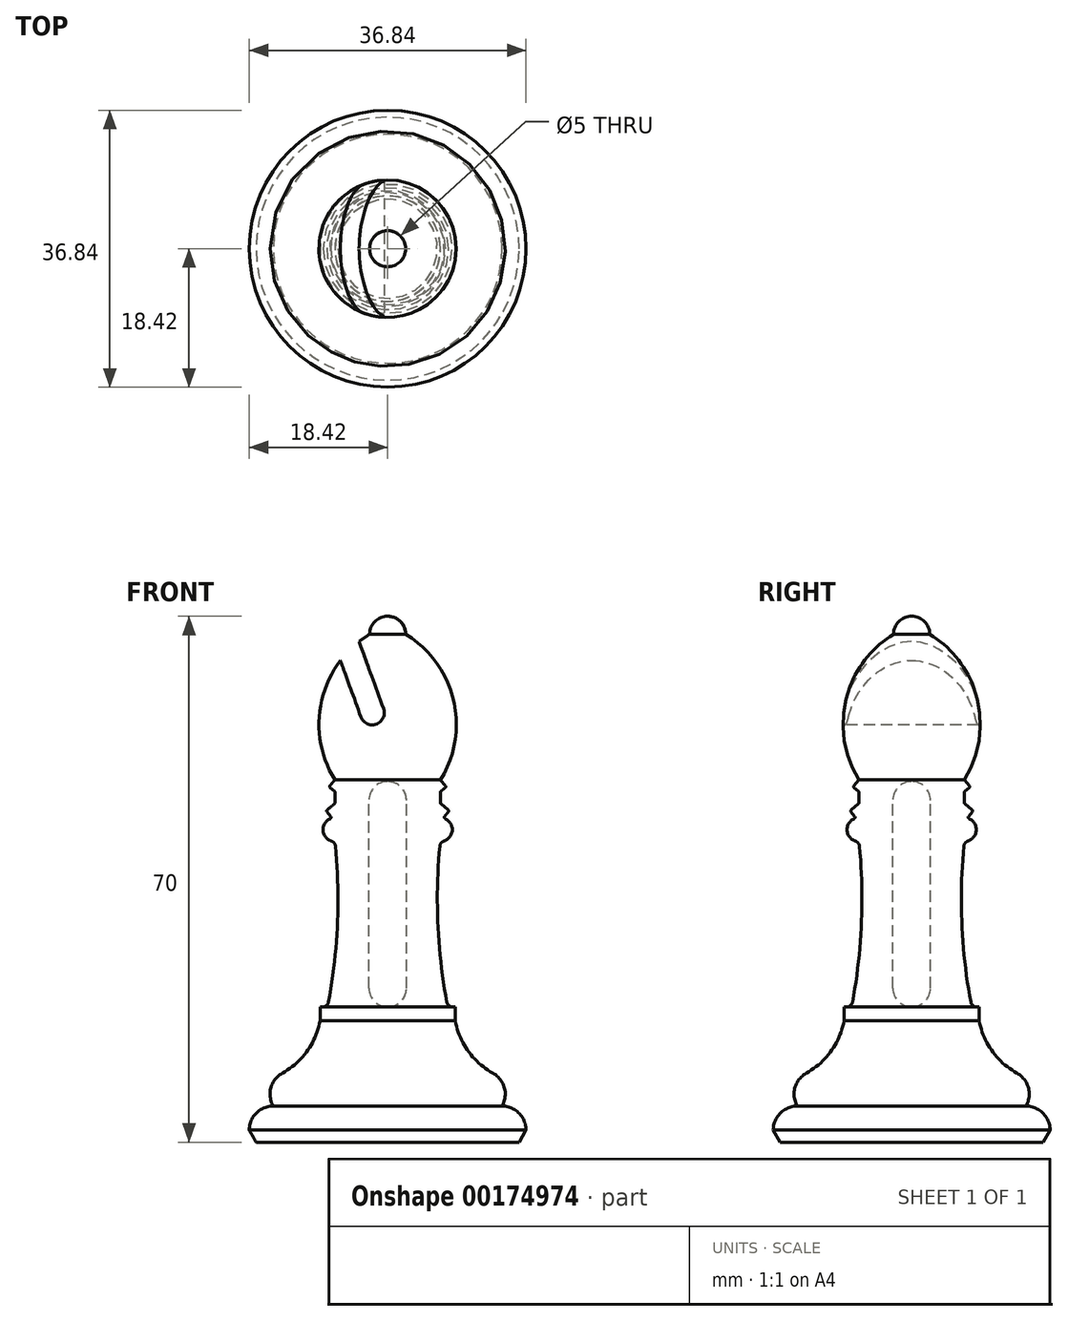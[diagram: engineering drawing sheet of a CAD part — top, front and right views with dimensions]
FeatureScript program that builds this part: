
annotation { "Feature Type Name" : "Feature", "Feature Type Description" : "" }
export const myFeature = defineFeature(function(context is Context, id is Id, definition is map)
    precondition{}
    {
        {
            var Q0;
            Q0=qCreatedBy(makeId("Front.planeOp"),FACE);
            var sketch = newSketch(context, id + "F0", { "sketchPlane" : qUnion([Q0])});
            skLineSegment(sketch, "E0", {"start": v(0, 0) * mm, "end": v(17.5, 0) * mm});
            skLineSegment(sketch, "E1", {"start": v(0, 0) * mm, "end": v(0, 95) * mm, "construction": true});
            skLineSegment(sketch, "E2", {"start": v(0, 18) * mm, "end": v(9, 18) * mm, "construction": true});
            skLineSegment(sketch, "E3", {"start": v(14.4, 40) * mm, "end": v(0, 40) * mm, "construction": true});
            skLineSegment(sketch, "E4", {"start": v(0, 60) * mm, "end": v(12.7, 60) * mm, "construction": true});
            skLineSegment(sketch, "E5", {"start": v(0, 64.34) * mm, "end": v(14.8, 64.34) * mm, "construction": true});
            skLineSegment(sketch, "E6", {"start": v(17.5, 0) * mm, "end": v(18.42, 1.6) * mm});
            skArc(sketch, "E7", {"start": v(18.42, 1.6) * mm, "mid": v(17.49, 3.86) * mm, "end": v(15.22, 4.8) * mm});
            skLineSegment(sketch, "E8", {"start": v(9, 18) * mm, "end": v(9, 16.15) * mm});
            skArc(sketch, "E9", {"start": v(9, 16.15) * mm, "mid": v(10.72, 12.11) * mm, "end": v(14, 9.2) * mm});
            skArc(sketch, "E10", {"start": v(15.22, 4.8) * mm, "mid": v(15.54, 7.26) * mm, "end": v(14, 9.2) * mm});
            skLineSegment(sketch, "E11", {"start": v(9, 18) * mm, "end": v(8, 18) * mm});
            skArc(sketch, "E12", {"start": v(7, 40) * mm, "mid": v(6.69, 28.96) * mm, "end": v(8, 18) * mm});
            skArc(sketch, "E13", {"start": v(7, 40) * mm, "mid": v(8.59, 41.4) * mm, "end": v(7.4, 43.15) * mm});
            skLineSegment(sketch, "E14", {"start": v(7.4, 43.15) * mm, "end": v(8.2, 44.1) * mm});
            skLineSegment(sketch, "E15", {"start": v(8.2, 44.1) * mm, "end": v(7, 45.1) * mm});
            skLineSegment(sketch, "E16", {"start": v(7, 45.1) * mm, "end": v(7, 46.63) * mm});
            skLineSegment(sketch, "E17", {"start": v(7, 46.63) * mm, "end": v(7.8, 47.3) * mm});
            skLineSegment(sketch, "E18", {"start": v(7.8, 47.3) * mm, "end": v(7, 48.26) * mm});
            skLineSegment(sketch, "E19", {"start": v(3.2, 63.2) * mm, "end": v(0, 63.2) * mm});
            skLineSegment(sketch, "E20", {"start": v(0, 63.2) * mm, "end": v(0, 0) * mm});
            skArc(sketch, "E21", {"start": v(7, 48.26) * mm, "mid": v(6.78, 56.16) * mm, "end": v(3.2, 63.2) * mm});
            skSolve(sketch);
        }
        {
            var Q0;
            Q0=qSketchRegion(id+"F0",true);
            var Q1;
            Q1=sQuery(id+"F0.wireOp",EDGE,"E1");
            revolve(context, id + "F1", {"entities" : qUnion([Q0]), "axis" : qUnion([Q1]), "revolveType" : RevolveType.FULL});
        }
        {
            var Q0;
            Q0=makeQuery(id+"F1.opRevolve","SWEPT_EDGE",EDGE,{"disambiguationData":[OSD([sQuery(id+"F0.wireOp",EDGE,"E12"),sQuery(id+"F0.wireOp",EDGE,"E13")])]});
            var Q1;
            Q1=makeQuery(id+"F1.opRevolve","SWEPT_EDGE",EDGE,{"disambiguationData":[OSD([sQuery(id+"F0.wireOp",EDGE,"E11"),sQuery(id+"F0.wireOp",EDGE,"E12")])]});
            fillet(context, id + "F2", {"entities" : qUnion([Q0, Q1]), "radius" : .8 * mm, "tangentPropagation" : true, "allowEdgeOverflow" : false});
        }
        {
            var Q0;
            Q0=makeQuery(id+"F1.opRevolve","SWEPT_EDGE",EDGE,{"disambiguationData":[OSD([sQuery(id+"F0.wireOp",EDGE,"E17"),sQuery(id+"F0.wireOp",EDGE,"E18")])]});
            var Q1;
            Q1=makeQuery(id+"F1.opRevolve","SWEPT_EDGE",EDGE,{"disambiguationData":[OSD([sQuery(id+"F0.wireOp",EDGE,"E14"),sQuery(id+"F0.wireOp",EDGE,"E15")])]});
            var Q2;
            Q2=makeQuery(id+"F1.opRevolve","SWEPT_EDGE",EDGE,{"disambiguationData":[OSD([sQuery(id+"F0.wireOp",EDGE,"OAx1KunF-KjKq-zgV9-Glhn-Sdbq04AqaJ7j"),sQuery(id+"F0.wireOp",EDGE,"E18")])]});
            var Q3;
            Q3=makeQuery(id+"F1.opRevolve","SWEPT_EDGE",EDGE,{"disambiguationData":[OSD([sQuery(id+"F0.wireOp",EDGE,"E16"),sQuery(id+"F0.wireOp",EDGE,"E17")])]});
            var Q4;
            Q4=makeQuery(id+"F1.opRevolve","SWEPT_EDGE",EDGE,{"disambiguationData":[OSD([sQuery(id+"F0.wireOp",EDGE,"E15"),sQuery(id+"F0.wireOp",EDGE,"E16")])]});
            var Q5;
            Q5=makeQuery(id+"F1.opRevolve","SWEPT_EDGE",EDGE,{"disambiguationData":[OSD([sQuery(id+"F0.wireOp",EDGE,"E13"),sQuery(id+"F0.wireOp",EDGE,"E14")])]});
            fillet(context, id + "F3", {"entities" : qUnion([Q0, Q1, Q2, Q3, Q4, Q5]), "radius" : .2 * mm, "tangentPropagation" : true, "allowEdgeOverflow" : false});
        }
        {
            var Q0;
            Q0=qCreatedBy(makeId("Front.planeOp"),FACE);
            var sketch = newSketch(context, id + "F4", { "sketchPlane" : qUnion([Q0])});
            skLineSegment(sketch, "E22.bottom", {"start": v(0, 18) * mm, "end": v(0, 18) * mm});
            skLineSegment(sketch, "E22.top", {"start": v(0, 48) * mm, "end": v(0, 48) * mm});
            skLineSegment(sketch, "E22.left", {"start": v(2.5, 20.5) * mm, "end": v(2.5, 45.5) * mm});
            skPoint(sketch, "E22.middle", {"position": v(0, 33) * mm});
            skPoint(sketch, "E23.visualSharp", {"position": v(2.5, 48) * mm});
            skArc(sketch, "E23.filletArc", {"start": v(2.5, 45.5) * mm, "mid": v(1.77, 47.27) * mm, "end": v(0, 48) * mm});
            skPoint(sketch, "E24.visualSharp", {"position": v(-2.5, 48) * mm});
            skPoint(sketch, "E25.visualSharp", {"position": v(-2.5, 18) * mm});
            skPoint(sketch, "E26.visualSharp", {"position": v(2.5, 18) * mm});
            skArc(sketch, "E26.filletArc", {"start": v(0, 18) * mm, "mid": v(1.77, 18.73) * mm, "end": v(2.5, 20.5) * mm});
            skLineSegment(sketch, "E27", {"start": v(0, 48) * mm, "end": v(0, 18) * mm});
            skSolve(sketch);
        }
        {
            var Q0;
            Q0=qSketchRegion(id+"F4",true);
            var Q1;
            Q1=qConstructionFilter(qBodyType(qCreatedBy(id+"F4",EDGE),BodyType.WIRE),ConstructionObject.NO);
            var Q2;
            Q2=sQuery(id+"F4.wireOp",EDGE,"E27");
            revolve(context, id + "F5", {"operationType" : NewBodyOperationType.REMOVE, "entities" : qUnion([Q0]), "surfaceEntities" : qUnion([Q1]), "axis" : qUnion([Q2]), "revolveType" : RevolveType.FULL});
        }
        {
            var Q0;
            Q0=qCreatedBy(makeId("Front.planeOp"),FACE);
            var sketch = newSketch(context, id + "F6", { "sketchPlane" : qUnion([Q0])});
            skLineSegment(sketch, "E28", {"start": v(0, 70) * mm, "end": v(0, 57.2) * mm});
            skArc(sketch, "E29", {"start": v(0, 70) * mm, "mid": v(1.7, 69.3) * mm, "end": v(2.4, 67.6) * mm});
            skLineSegment(sketch, "E30", {"start": v(7, 48.18) * mm, "end": v(0, 48.18) * mm});
            skLineSegment(sketch, "E31", {"start": v(0, 48.18) * mm, "end": v(0, 57.2) * mm});
            skArc(sketch, "E32", {"start": v(7, 48.18) * mm, "mid": v(8.77, 58.85) * mm, "end": v(2.4, 67.6) * mm});
            skSolve(sketch);
        }
        {
            var Q0;
            Q0=qSketchRegion(id+"F6",true);
            var Q1;
            Q1=sQuery(id+"F6.wireOp",EDGE,"E28");
            revolve(context, id + "F7", {"operationType" : NewBodyOperationType.ADD, "entities" : qUnion([Q0]), "axis" : qUnion([Q1]), "revolveType" : RevolveType.FULL});
        }
        {
            var Q0;
            Q0=qCreatedBy(makeId("Front.planeOp"),FACE);
            var sketch = newSketch(context, id + "F8", { "sketchPlane" : qUnion([Q0])});
            skLineSegment(sketch, "E33", {"start": v(-7.11, 66.36) * mm, "end": v(-3.55, 56.6) * mm});
            skLineSegment(sketch, "E34", {"start": v(-1.5, 55.64) * mm, "end": v(-1.5, 55.64) * mm});
            skLineSegment(sketch, "E35", {"start": v(-0.55, 57.69) * mm, "end": v(-4.1, 67.46) * mm});
            skLineSegment(sketch, "E36", {"start": v(-4.1, 67.46) * mm, "end": v(-7.11, 66.36) * mm});
            skPoint(sketch, "E37.visualSharp", {"position": v(-3, 55.09) * mm});
            skArc(sketch, "E37.filletArc", {"start": v(-3.55, 56.6) * mm, "mid": v(-2.73, 55.69) * mm, "end": v(-1.5, 55.64) * mm});
            skPoint(sketch, "E38.visualSharp", {"position": v(0, 56.18) * mm});
            skArc(sketch, "E38.filletArc", {"start": v(-1.5, 55.64) * mm, "mid": v(-0.6, 56.46) * mm, "end": v(-0.55, 57.69) * mm});
            skSolve(sketch);
        }
        {
            var Q0;
            Q0 = qSketchRegion(id + "F8", true);
            extrude(context, id + "F9", {"entities" : qUnion([Q0]), "operationType" : NewBodyOperationType.REMOVE, "oppositeDirection" : true, "depth" : 25 * mm, "symmetric" : true});
        }
    });
